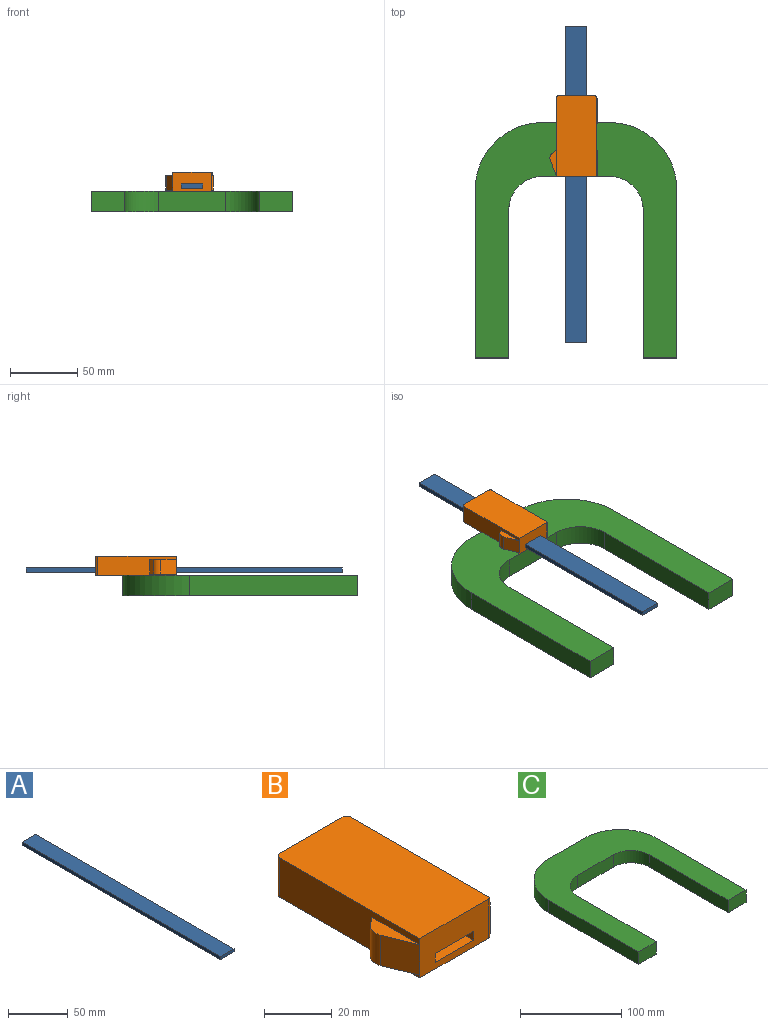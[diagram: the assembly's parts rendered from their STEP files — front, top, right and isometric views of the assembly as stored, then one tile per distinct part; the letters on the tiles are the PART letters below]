
ASSEMBLY  parts=3 mates=2
PART A: 6 faces, bbox 16x235x3.2 mm
  f0: plane 235x3.2mm, normal (-1,0,0), area 752mm2, adj f1,f3,f4,f5
  f1: plane 16x3.2mm, normal (0,-1,0), area 51.2mm2, adj f0,f2,f4,f5
  f2: plane 235x3.2mm, normal (1,0,0), area 752mm2, adj f1,f3,f4,f5
  f3: plane 16x3.2mm, normal (0,1,0), area 51.2mm2, adj f0,f2,f4,f5
  f4: plane 235x16mm, normal (0,0,1), area 3760mm2, adj f0,f1,f2,f3
  f5: plane 235x16mm, normal (0,0,-1), area 3760mm2, adj f0,f1,f2,f3
PART B: 27 faces, bbox 35.2x60x14.2 mm
  f0: plane 58.5x14.2mm, normal (-1,0,0), area 610.7mm2, adj f1,f4,f5,f10,f13,f14,f25
  f1: plane 28.7x14.2mm, normal (0,-1,0), area 356.3mm2, adj f0,f4,f5,f6,f7,f8,f9,f12
  f2: plane 58.27x14.2mm, normal (1,0,0), area 412mm2, adj f4,f5,f15,f17,f18,f19,f21,f22
  f3: plane 26.5x14.2mm, normal (0,1,0), area 325.1mm2, adj f4,f5,f6,f7,f8,f9,f24,f25
  f4: plane 60x29.5mm, normal (0,0,1), area 1769mm2, adj f0,f1,f2,f3,f24,f25,f26
  f5: plane 60x29.5mm, normal (0,0,-1), area 1769mm2, adj f0,f1,f2,f3,f24,f25,f26
  f6: plane 60x3.2mm, normal (1,0,0), area 192mm2, adj f1,f3,f7,f9
  f7: plane 60x16mm, normal (0,0,1), area 960mm2, adj f1,f3,f6,f8
  f8: plane 60x3.2mm, normal (-1,0,0), area 192mm2, adj f1,f3,f7,f9
  f9: plane 60x16mm, normal (0,0,-1), area 960mm2, adj f1,f3,f6,f8
  f10: plane 11x3.21mm, normal (-0.64,0.77,0), area 46mm2, adj f0,f11,f13,f14
  f11: cylinder r=5mm len=11mm, axis (0,0,-1), area 69.1mm2, adj f10,f12,f13,f14
  f12: plane 11.63x11mm, normal (-0.93,-0.37,0), area 137.8mm2, adj f1,f11,f13,f14
  f13: plane 20x5.01mm, normal (0,0,1), area 57.5mm2, adj f0,f10,f11,f12
  f14: plane 20x5.01mm, normal (0,0,-1), area 57.5mm2, adj f0,f10,f11,f12
  f15: plane 11x0.7mm, normal (0,-1,0), area 7.7mm2, adj f2,f16,f18,f19
  f16: plane 19x11mm, normal (1,0,0), area 209mm2, adj f15,f17,f18,f19
  f17: plane 11x0.7mm, normal (0,1,0), area 7.7mm2, adj f2,f16,f18,f19
  f18: plane 19x0.7mm, normal (0,0,1), area 13.3mm2, adj f2,f15,f16,f17
  f19: plane 19x0.7mm, normal (0,0,-1), area 13.3mm2, adj f2,f15,f16,f17
  f20: plane 17.5x11mm, normal (1,0,0), area 192.5mm2, adj f21,f22,f23,f26
  f21: plane 11x0.7mm, normal (0,1,0), area 7.7mm2, adj f2,f20,f22,f23
  f22: plane 18.77x0.7mm, normal (0,0,1), area 12.9mm2, adj f2,f20,f21,f26
  f23: plane 18.77x0.7mm, normal (0,0,-1), area 12.9mm2, adj f2,f20,f21,f26
  f24: cylinder r=1.5mm len=14.2mm, axis (0,0,-1), area 33.5mm2, adj f2,f3,f4,f5
  f25: cylinder r=1.5mm len=14.2mm, axis (0,0,-1), area 33.5mm2, adj f0,f3,f4,f5
  f26: cylinder r=1.5mm len=14.2mm, axis (0,0,1), area 28.6mm2, adj f1,f2,f4,f5,f20,f22,f23
PART C: 14 faces, bbox 150x175x15 mm
  f0: cylinder r=50mm len=50mm, axis (0,0,-1), area 1178.1mm2, adj f1,f11,f12,f13
  f1: plane 125x15mm, normal (-1,0,0), area 1875mm2, adj f0,f2,f12,f13
  f2: plane 25x15mm, normal (0,-1,0), area 375mm2, adj f1,f3,f12,f13
  f3: plane 110x15mm, normal (1,0,0), area 1650mm2, adj f2,f4,f12,f13
  f4: cylinder r=25mm len=25mm, axis (0,0,-1), area 589mm2, adj f3,f5,f12,f13
  f5: plane 50x15mm, normal (0,-1,0), area 750mm2, adj f4,f6,f12,f13
  f6: cylinder r=25mm len=25mm, axis (0,0,-1), area 589mm2, adj f5,f7,f12,f13
  f7: plane 110x15mm, normal (-1,0,0), area 1650mm2, adj f6,f8,f12,f13
  f8: plane 25x15mm, normal (0,-1,0), area 375mm2, adj f7,f9,f12,f13
  f9: plane 125x15mm, normal (1,0,0), area 1875mm2, adj f8,f10,f12,f13
  f10: cylinder r=50mm len=50mm, axis (0,0,-1), area 1178.1mm2, adj f9,f11,f12,f13
  f11: plane 50x15mm, normal (0,1,0), area 750mm2, adj f0,f10,f12,f13
  f12: plane 175x150mm, normal (0,0,1), area 11945.2mm2, adj f0,f1,f2,f3,f4,f5,f6,f7
  f13: plane 175x150mm, normal (0,0,-1), area 11945.2mm2, adj f0,f1,f2,f3,f4,f5,f6,f7
PLACE A t=(-6,-153.14,-4.74)mm
PLACE B t=(-12.5,-29.97,-7.14)mm fixed
PLACE C t=(1.85,-29.97,-22.14)mm
MATE fastened C.f12 <-> B.f5  axis (0,0,1) through (1.85,-29.97,-7.14)mm
MATE slider B.f1 <-> A.f1  axis (0,-1,0) through (10,-29.97,-1.54)mm
